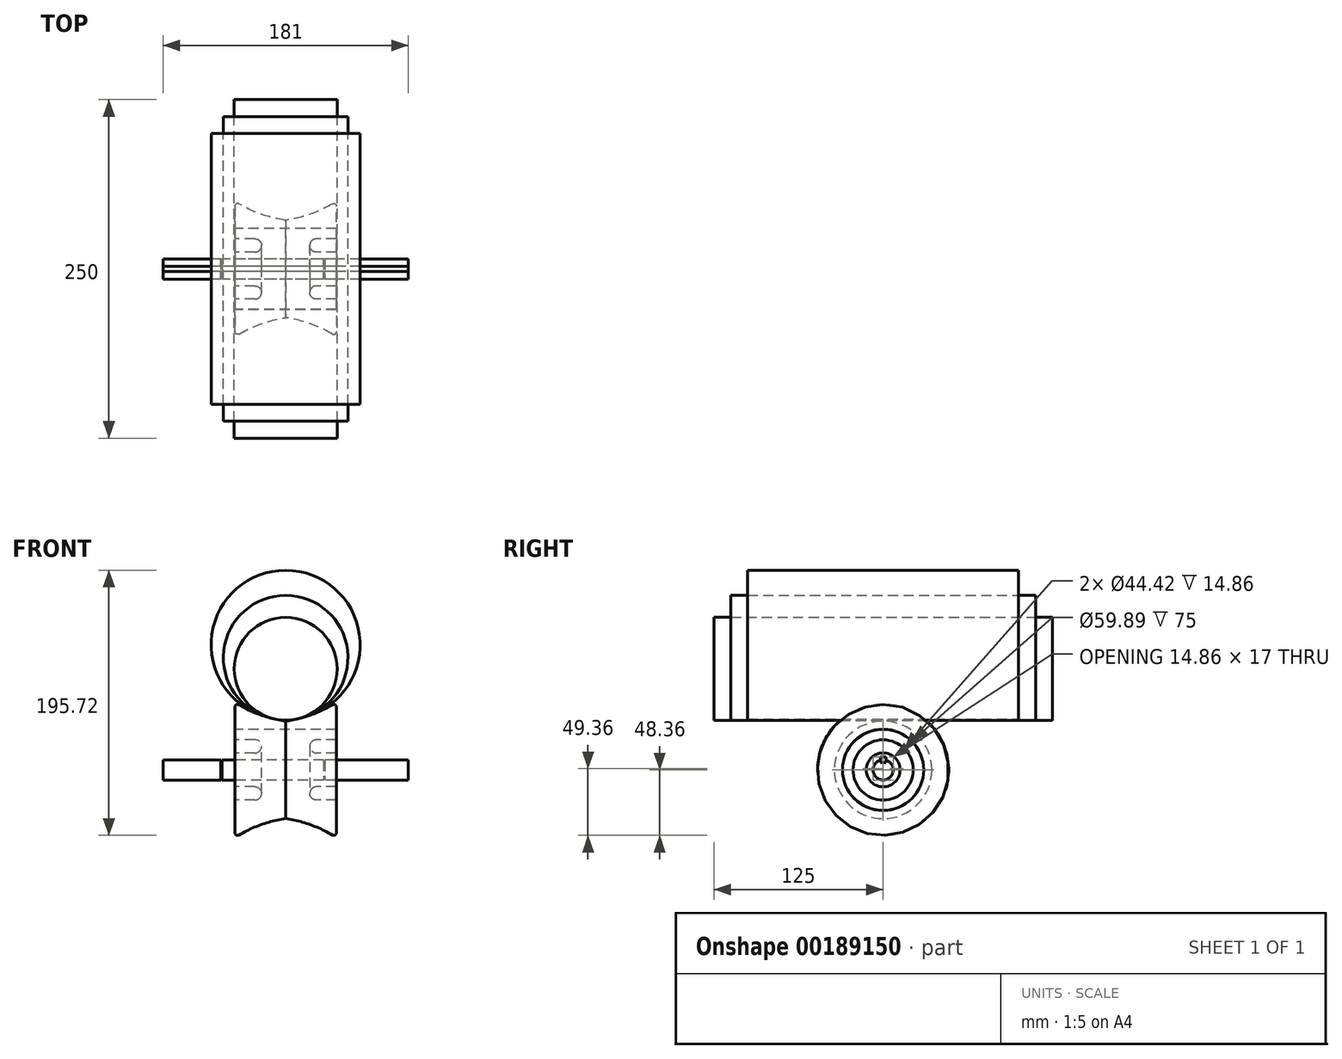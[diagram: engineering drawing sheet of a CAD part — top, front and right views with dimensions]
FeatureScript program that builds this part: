
annotation { "Feature Type Name" : "Feature", "Feature Type Description" : "" }
export const myFeature = defineFeature(function(context is Context, id is Id, definition is map)
    precondition{}
    {
        {
            var Q0;
            Q0=qCreatedBy(makeId("Front.planeOp"),FACE);
            var sketch = newSketch(context, id + "F0", { "sketchPlane" : qUnion([Q0])});
            skLineSegment(sketch, "E0", {"start": v(0, 0) * mm, "end": v(0, 7.5) * mm, "construction": true});
            skLineSegment(sketch, "E1", {"start": v(0, 7.5) * mm, "end": v(28, 7.5) * mm, "construction": true});
            skLineSegment(sketch, "E2", {"start": v(90.5, 7.5) * mm, "end": v(90.5, 0) * mm, "construction": true});
            skLineSegment(sketch, "E3", {"start": v(90.5, 0) * mm, "end": v(0, 0) * mm, "construction": true});
            skLineSegment(sketch, "E4.MirrorCS", {"start": v(0, 7.5) * mm, "end": v(-47, 7.5) * mm, "construction": true});
            skLineSegment(sketch, "E5.MirrorCS", {"start": v(-90.5, 7.5) * mm, "end": v(-90.5, 0) * mm, "construction": true});
            skLineSegment(sketch, "E6.MirrorCS", {"start": v(-90.5, 0) * mm, "end": v(0, 0) * mm, "construction": true});
            skLineSegment(sketch, "E7", {"start": v(-90.5, 0) * mm, "end": v(-90.5, 7.5) * mm});
            skLineSegment(sketch, "E8", {"start": v(90.5, 7.5) * mm, "end": v(90.5, 0) * mm});
            skLineSegment(sketch, "E9", {"start": v(-90.5, 7.5) * mm, "end": v(-48, 7.5) * mm});
            skLineSegment(sketch, "E10", {"start": v(-90.5, 0) * mm, "end": v(90.5, 0) * mm});
            skLineSegment(sketch, "E11", {"start": v(-9.5, 7.5) * mm, "end": v(-9.5, 0) * mm, "construction": true});
            skLineSegment(sketch, "E12", {"start": v(-47.5, 7) * mm, "end": v(-47.5, 0) * mm, "construction": true});
            skLineSegment(sketch, "E13", {"start": v(28.5, 7) * mm, "end": v(28.5, 0) * mm, "construction": true});
            skLineSegment(sketch, "E14", {"start": v(-48, 7.5) * mm, "end": v(-48, 7) * mm});
            skLineSegment(sketch, "E15", {"start": v(-48, 7) * mm, "end": v(-47, 7) * mm});
            skLineSegment(sketch, "E16", {"start": v(-47, 7) * mm, "end": v(-47, 7.5) * mm});
            skLineSegment(sketch, "E17.trimOffspring", {"start": v(-48, 7.5) * mm, "end": v(-90.5, 7.5) * mm, "construction": true});
            skLineSegment(sketch, "E18.trimOffspring", {"start": v(-47, 7.5) * mm, "end": v(28, 7.5) * mm});
            skPoint(sketch, "E19.orphan", {"position": v(-47.5, 7.5) * mm});
            skLineSegment(sketch, "E20", {"start": v(28, 7.5) * mm, "end": v(28, 7) * mm});
            skLineSegment(sketch, "E21", {"start": v(28, 7) * mm, "end": v(29, 7) * mm});
            skLineSegment(sketch, "E22", {"start": v(29, 7) * mm, "end": v(29, 7.5) * mm});
            skLineSegment(sketch, "E23.trimOffspring", {"start": v(29, 7.5) * mm, "end": v(90.5, 7.5) * mm, "construction": true});
            skLineSegment(sketch, "E24.trimOffspring", {"start": v(29, 7.5) * mm, "end": v(90.5, 7.5) * mm});
            skPoint(sketch, "E25.orphan", {"position": v(28.5, 7.5) * mm});
            skSolve(sketch);
        }
        {
            var Q0;
            Q0=qSketchRegion(id+"F0",true);
            var Q1;
            Q1=sQuery(id+"F0.wireOp",EDGE,"E10");
            revolve(context, id + "F1", {"entities" : qUnion([Q0]), "axis" : qUnion([Q1]), "revolveType" : RevolveType.FULL});
        }
        {
            var Q0;
            Q0=makeQuery(id+"F1.opRevolve","SWEPT_FACE",FACE,{"disambiguationData":[OSD([sQuery(id+"F0.wireOp",EDGE,"E7")])]});
            var sketch = newSketch(context, id + "F2", { "sketchPlane" : qUnion([Q0])});
            skLineSegment(sketch, "E26", {"start": v(0, 7.5) * mm, "end": v(0, 5.5) * mm, "construction": true});
            skLineSegment(sketch, "E27", {"start": v(0, 5.5) * mm, "end": v(2, 5.5) * mm, "construction": true});
            skLineSegment(sketch, "E28", {"start": v(2, 5.5) * mm, "end": v(2, 7.23) * mm, "construction": true});
            skLineSegment(sketch, "E29", {"start": v(0, 5.5) * mm, "end": v(-2, 5.5) * mm, "construction": true});
            skLineSegment(sketch, "E30", {"start": v(-2, 5.5) * mm, "end": v(-2, 7.23) * mm, "construction": true});
            skLineSegment(sketch, "E31", {"start": v(-2, 7.23) * mm, "end": v(-2, 5.5) * mm});
            skLineSegment(sketch, "E32", {"start": v(2, 5.5) * mm, "end": v(2, 7.23) * mm});
            skLineSegment(sketch, "E33", {"start": v(-2, 5.5) * mm, "end": v(2, 5.5) * mm});
            skLineSegment(sketch, "E34", {"start": v(-2, 5.5) * mm, "end": v(-2, 7.23) * mm});
            skSolve(sketch);
        }
        {
            var Q0;
            Q0=makeQuery(id+"F2.imprint","IMPRINT",FACE,{"disambiguationData":[TD([[makeQuery(id+"F2.imprint","IMPRINT",EDGE,{"derivedFrom":sQuery(id+"F2.wireOp",EDGE,"E33")}),1.0]])]});
            extrude(context, id + "F3", {"entities" : qUnion([Q0]), "operationType" : NewBodyOperationType.REMOVE, "endBound" : BoundingType.THROUGH_ALL, "oppositeDirection" : true, "depth" : 25 * mm});
        }
        {
            var Q0;
            Q0=qCreatedBy(makeId("Front.planeOp"),FACE);
            var sketch = newSketch(context, id + "F4", { "sketchPlane" : qUnion([Q0])});
            skLineSegment(sketch, "E35", {"start": v(0, 7.5) * mm, "end": v(37.5, 7.5) * mm});
            skLineSegment(sketch, "E36", {"start": v(37.5, 7.5) * mm, "end": v(37.5, 12.5) * mm});
            skLineSegment(sketch, "E37", {"start": v(37.5, 12.5) * mm, "end": v(22.64, 12.5) * mm});
            skLineSegment(sketch, "E38", {"start": v(0, 0) * mm, "end": v(0, 30) * mm, "construction": true});
            skArc(sketch, "E39", {"start": v(22.64, 22.21) * mm, "mid": v(17.78, 17.36) * mm, "end": v(22.64, 12.5) * mm});
            skLineSegment(sketch, "E40", {"start": v(37.5, 30) * mm, "end": v(37.5, 22.21) * mm});
            skLineSegment(sketch, "E41", {"start": v(37.5, 22.21) * mm, "end": v(22.64, 22.21) * mm});
            skLineSegment(sketch, "E42", {"start": v(0, 30) * mm, "end": v(37.5, 30) * mm});
            skLineSegment(sketch, "E43.MirrorCS", {"start": v(0, 30) * mm, "end": v(-37.5, 30) * mm});
            skLineSegment(sketch, "E44.MirrorCS", {"start": v(-37.5, 30) * mm, "end": v(-37.5, 22.21) * mm});
            skLineSegment(sketch, "E45.MirrorCS", {"start": v(-37.5, 22.21) * mm, "end": v(-22.64, 22.21) * mm});
            skArc(sketch, "E46.MirrorCS", {"start": v(-22.64, 22.21) * mm, "mid": v(-17.78, 17.36) * mm, "end": v(-22.64, 12.5) * mm});
            skLineSegment(sketch, "E47.MirrorCS", {"start": v(-37.5, 12.5) * mm, "end": v(-22.64, 12.5) * mm});
            skLineSegment(sketch, "E48.MirrorCS", {"start": v(-37.5, 7.5) * mm, "end": v(-37.5, 12.5) * mm});
            skLineSegment(sketch, "E49.MirrorCS", {"start": v(0, 7.5) * mm, "end": v(-37.5, 7.5) * mm});
            skSolve(sketch);
        }
        {
            var Q0;
            Q0=makeQuery(id+"F4.imprint","IMPRINT",FACE,{"disambiguationData":[TD([[makeQuery(id+"F4.imprint","IMPRINT",EDGE,{"derivedFrom":sQuery(id+"F4.wireOp",EDGE,"E35")}),1.0]])]});
            var Q1;
            Q1=sQuery(id+"F0.wireOp",EDGE,"E10");
            revolve(context, id + "F5", {"entities" : qUnion([Q0]), "axis" : qUnion([Q1]), "revolveType" : RevolveType.FULL});
        }
        {
            var Q0;
            Q0=makeQuery(id+"F5.opRevolve","SWEPT_FACE",FACE,{"disambiguationData":[OSD([sQuery(id+"F4.wireOp",EDGE,"E48.MirrorCS")])]});
            var sketch = newSketch(context, id + "F6", { "sketchPlane" : qUnion([Q0])});
            skLineSegment(sketch, "E50", {"start": v(0, 7.5) * mm, "end": v(0, 9.5) * mm, "construction": true});
            skLineSegment(sketch, "E51", {"start": v(0, 9.5) * mm, "end": v(0.2, 9.5) * mm, "construction": true});
            skLineSegment(sketch, "E52", {"start": v(2, 9.5) * mm, "end": v(0, 9.5) * mm, "construction": true});
            skLineSegment(sketch, "E53", {"start": v(0, 9.5) * mm, "end": v(-2, 9.5) * mm, "construction": true});
            skLineSegment(sketch, "E54", {"start": v(-2, 9.5) * mm, "end": v(2, 9.5) * mm});
            skLineSegment(sketch, "E55", {"start": v(2, 7.23) * mm, "end": v(2, 9.5) * mm});
            skLineSegment(sketch, "E56", {"start": v(-2, 9.5) * mm, "end": v(-2, 7.23) * mm});
            skSolve(sketch);
        }
        {
            var Q0;
            Q0=qSketchRegion(id+"F6",true);
            var Q1;
            Q1=makeQuery(id+"F6.imprint","IMPRINT",FACE,{"disambiguationData":[TD([[makeQuery(id+"F6.imprint","IMPRINT",EDGE,{"derivedFrom":sQuery(id+"F6.wireOp",EDGE,"E54")}),-1.0]])]});
            extrude(context, id + "F7", {"entities" : qUnion([Q0, Q1]), "operationType" : NewBodyOperationType.REMOVE, "endBound" : BoundingType.THROUGH_ALL, "oppositeDirection" : true, "depth" : 25 * mm});
        }
        {
            var Q0;
            Q0=qCreatedBy(makeId("Front.planeOp"),FACE);
            var sketch = newSketch(context, id + "F8", { "sketchPlane" : qUnion([Q0])});
            skLineSegment(sketch, "E57", {"start": v(0, 29.94) * mm, "end": v(-37.5, 29.94) * mm});
            skLineSegment(sketch, "E58", {"start": v(-37.5, 29.94) * mm, "end": v(-37.5, 49.94) * mm});
            skLineSegment(sketch, "E59", {"start": v(-37.5, 49.94) * mm, "end": v(37.5, 49.94) * mm});
            skLineSegment(sketch, "E60", {"start": v(37.5, 49.94) * mm, "end": v(37.5, 29.94) * mm});
            skLineSegment(sketch, "E61", {"start": v(37.5, 29.94) * mm, "end": v(0, 29.94) * mm});
            skArc(sketch, "E62", {"start": v(0, 36) * mm, "mid": v(19.5, 40.94) * mm, "end": v(37.5, 49.94) * mm});
            skArc(sketch, "E63.MirrorCS", {"start": v(0, 36) * mm, "mid": v(-19.5, 40.94) * mm, "end": v(-37.5, 49.94) * mm});
            skSolve(sketch);
        }
        {
            var Q0;
            Q0=makeQuery(id+"F8.imprint","IMPRINT",FACE,{"disambiguationData":[TD([[makeQuery(id+"F8.imprint","IMPRINT",EDGE,{"derivedFrom":sQuery(id+"F8.wireOp",EDGE,"E57")}),-1.0]])]});
            var Q1;
            Q1=sQuery(id+"F0.wireOp",EDGE,"E10");
            revolve(context, id + "F9", {"entities" : qUnion([Q0]), "axis" : qUnion([Q1]), "revolveType" : RevolveType.FULL});
        }
        {
            var Q0;
            Q0=makeQuery(id+"F9.opRevolve","SWEPT_EDGE",EDGE,{"disambiguationData":[OSD([sQuery(id+"F8.wireOp",EDGE,"E58"),sQuery(id+"F8.wireOp",EDGE,"E59")])]});
            var Q1;
            Q1=makeQuery(id+"F9.opRevolve","SWEPT_EDGE",EDGE,{"disambiguationData":[OSD([sQuery(id+"F8.wireOp",EDGE,"E59"),sQuery(id+"F8.wireOp",EDGE,"E60")])]});
            fillet(context, id + "F10", {"entities" : qUnion([Q0, Q1]), "radius" : 2 * mm, "tangentPropagation" : true, "allowEdgeOverflow" : false});
        }
        {
            var Q0;
            Q0=qCreatedBy(makeId("Front.planeOp"),FACE);
            var sketch = newSketch(context, id + "F11", { "sketchPlane" : qUnion([Q0])});
            skCircle(sketch, "E64", {"center": v(0, 74.64) * mm, "radius": 38 * mm});
            skSolve(sketch);
        }
        {
            var Q0;
            Q0=makeQuery(id+"F11.imprint","IMPRINT",FACE,{"disambiguationData":[TD([[makeQuery(id+"F11.imprint","IMPRINT",EDGE,{"derivedFrom":sQuery(id+"F11.wireOp",EDGE,"E64")}),1.0]])]});
            extrude(context, id + "F12", {"entities" : qUnion([Q0]), "endBound" : BoundingType.SYMMETRIC, "depth" : 250 * mm});
        }
        {
            var Q0;
            Q0=qCreatedBy(makeId("Front.planeOp"),FACE);
            var sketch = newSketch(context, id + "F13", { "sketchPlane" : qUnion([Q0])});
            skCircle(sketch, "E65", {"center": v(0, 82.91) * mm, "radius": 46 * mm});
            skSolve(sketch);
        }
        {
            var Q0;
            Q0 = qSketchRegion(id + "F13", true);
            extrude(context, id + "F14", {"entities" : qUnion([Q0]), "endBound" : BoundingType.SYMMETRIC, "depth" : 225 * mm});
        }
        {
            var Q0;
            Q0=qCreatedBy(makeId("Front.planeOp"),FACE);
            var sketch = newSketch(context, id + "F15", { "sketchPlane" : qUnion([Q0])});
            skCircle(sketch, "E66", {"center": v(0, 92.36) * mm, "radius": 55 * mm});
            skSolve(sketch);
        }
        {
            var Q0;
            Q0=makeQuery(id+"F15.imprint","IMPRINT",FACE,{"disambiguationData":[TD([[makeQuery(id+"F15.imprint","IMPRINT",EDGE,{"derivedFrom":sQuery(id+"F15.wireOp",EDGE,"E66")}),1.0]])]});
            extrude(context, id + "F16", {"entities" : qUnion([Q0]), "endBound" : BoundingType.SYMMETRIC, "depth" : 200 * mm});
        }
    });
